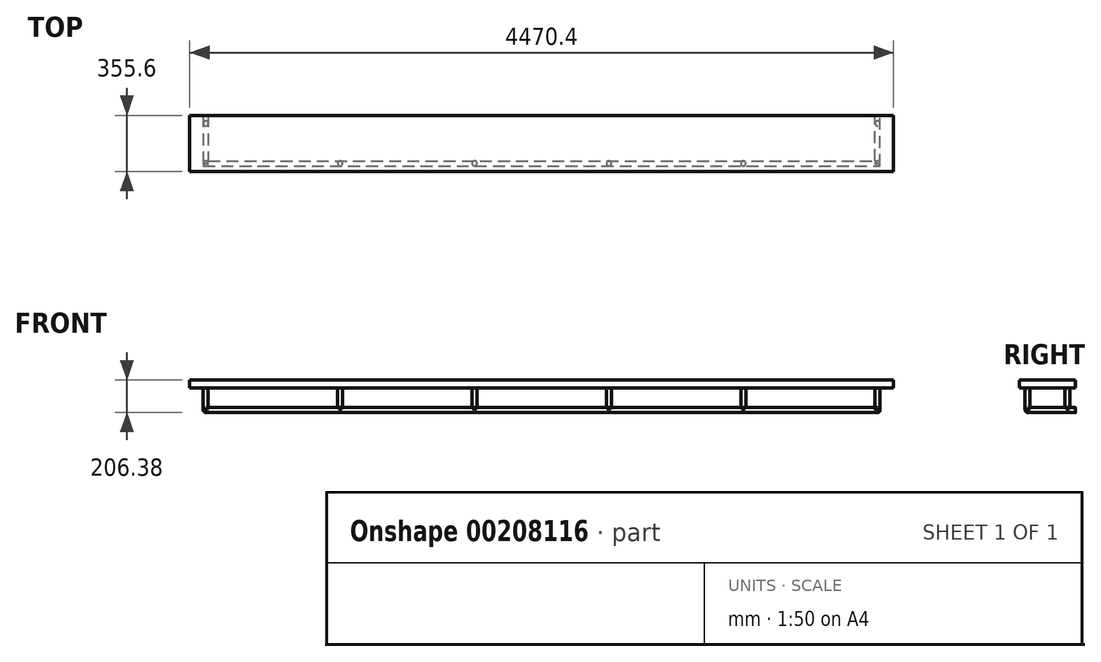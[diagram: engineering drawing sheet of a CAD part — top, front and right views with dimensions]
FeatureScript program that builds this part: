
annotation { "Feature Type Name" : "Feature", "Feature Type Description" : "" }
export const myFeature = defineFeature(function(context is Context, id is Id, definition is map)
    precondition{}
    {
        {
            var Q0;
            Q0=qCreatedBy(makeId("Top.planeOp"),FACE);
            var sketch = newSketch(context, id + "F0", { "sketchPlane" : qUnion([Q0])});
            skLineSegment(sketch, "E0", {"start": v(0, 0) * mm, "end": v(0, -304.8) * mm});
            skLineSegment(sketch, "E1", {"start": v(0, -304.8) * mm, "end": v(4267.2, -304.8) * mm});
            skLineSegment(sketch, "E2", {"start": v(4267.2, -304.8) * mm, "end": v(4267.2, 0) * mm});
            skSolve(sketch);
        }
        {
            var Q0;
            Q0=qCreatedBy(makeId("Front.planeOp"),FACE);
            var sketch = newSketch(context, id + "F1", { "sketchPlane" : qUnion([Q0])});
            skCircle(sketch, "E3", {"center": v(0, 0) * mm, "radius": 15.88 * mm});
            skSolve(sketch);
        }
        {
            var Q0;
            Q0=makeQuery(id+"F1.imprint","IMPRINT",FACE,{"disambiguationData":[TD([[makeQuery(id+"F1.imprint","IMPRINT",EDGE,{"derivedFrom":sQuery(id+"F1.wireOp",EDGE,"E3")}),1.0]])]});
            var Q1;
            Q1 = qConstructionFilter(qBodyType(qCreatedBy(id + "F0" ,EDGE), BodyType.WIRE), ConstructionObject.NO);
            sweep(context, id + "F2", {"profiles" : qUnion([Q0]), "path" : qUnion([Q1])});
        }
        {
            var Q0;
            Q0=qCreatedBy(makeId("Top.planeOp"),FACE);
            cPlane(context, id + "F3", {"entities" : qUnion([Q0]), "cplaneType" : CPlaneType.OFFSET, "offset" : 139.7 * mm, "width" : 152.4 * mm, "height" : 152.4 * mm});
        }
        {
            var Q0;
            Q0=qCreatedBy(id+"F3.planeOp",FACE);
            var sketch = newSketch(context, id + "F4", { "sketchPlane" : qUnion([Q0])});
            skCircle(sketch, "E4", {"center": v(0, -50.8) * mm, "radius": 15.87 * mm});
            skCircle(sketch, "E5", {"center": v(0, -304.8) * mm, "radius": 15.88 * mm});
            skCircle(sketch, "E6", {"center": v(4267.2, -50.8) * mm, "radius": 15.88 * mm});
            skCircle(sketch, "E7", {"center": v(4267.2, -304.8) * mm, "radius": 15.88 * mm});
            skCircle(sketch, "E8", {"center": v(853.44, -304.8) * mm, "radius": 15.88 * mm});
            skCircle(sketch, "E9", {"center": v(1706.88, -304.8) * mm, "radius": 15.88 * mm});
            skCircle(sketch, "E10", {"center": v(2560.32, -304.8) * mm, "radius": 15.88 * mm});
            skCircle(sketch, "E11", {"center": v(3413.76, -304.8) * mm, "radius": 15.88 * mm});
            skSolve(sketch);
        }
        {
            var Q0;
            Q0 = qSketchRegion(id + "F4", true);
            extrude(context, id + "F5", {"entities" : qUnion([Q0]), "endBound" : BoundingType.UP_TO_NEXT, "oppositeDirection" : true, "depth" : 25.4 * mm});
        }
        {
            var Q0;
            Q0=qCreatedBy(makeId("Right.planeOp"),FACE);
            cPlane(context, id + "F6", {"entities" : qUnion([Q0]), "cplaneType" : CPlaneType.OFFSET, "offset" : 101.6 * mm, "oppositeDirection" : true, "width" : 152.4 * mm, "height" : 152.4 * mm});
        }
        {
            var Q0;
            Q0=qCreatedBy(id+"F6.planeOp",FACE);
            var sketch = newSketch(context, id + "F7", { "sketchPlane" : qUnion([Q0])});
            skLineSegment(sketch, "E12.bottom", {"start": v(0, 139.7) * mm, "end": v(-355.6, 139.7) * mm});
            skLineSegment(sketch, "E12.top", {"start": v(0, 190.5) * mm, "end": v(-355.6, 190.5) * mm});
            skLineSegment(sketch, "E12.left", {"start": v(0, 139.7) * mm, "end": v(0, 190.5) * mm});
            skLineSegment(sketch, "E12.right", {"start": v(-355.6, 139.7) * mm, "end": v(-355.6, 190.5) * mm});
            skSolve(sketch);
        }
        {
            var Q0;
            Q0=makeQuery(id+"F7.imprint","IMPRINT",FACE,{"disambiguationData":[TD([[makeQuery(id+"F7.imprint","IMPRINT",EDGE,{"derivedFrom":sQuery(id+"F7.wireOp",EDGE,"E12.bottom")}),-1.0]])]});
            extrude(context, id + "F8", {"entities" : qUnion([Q0]), "depth" : 4470.4 * mm});
        }
    });
